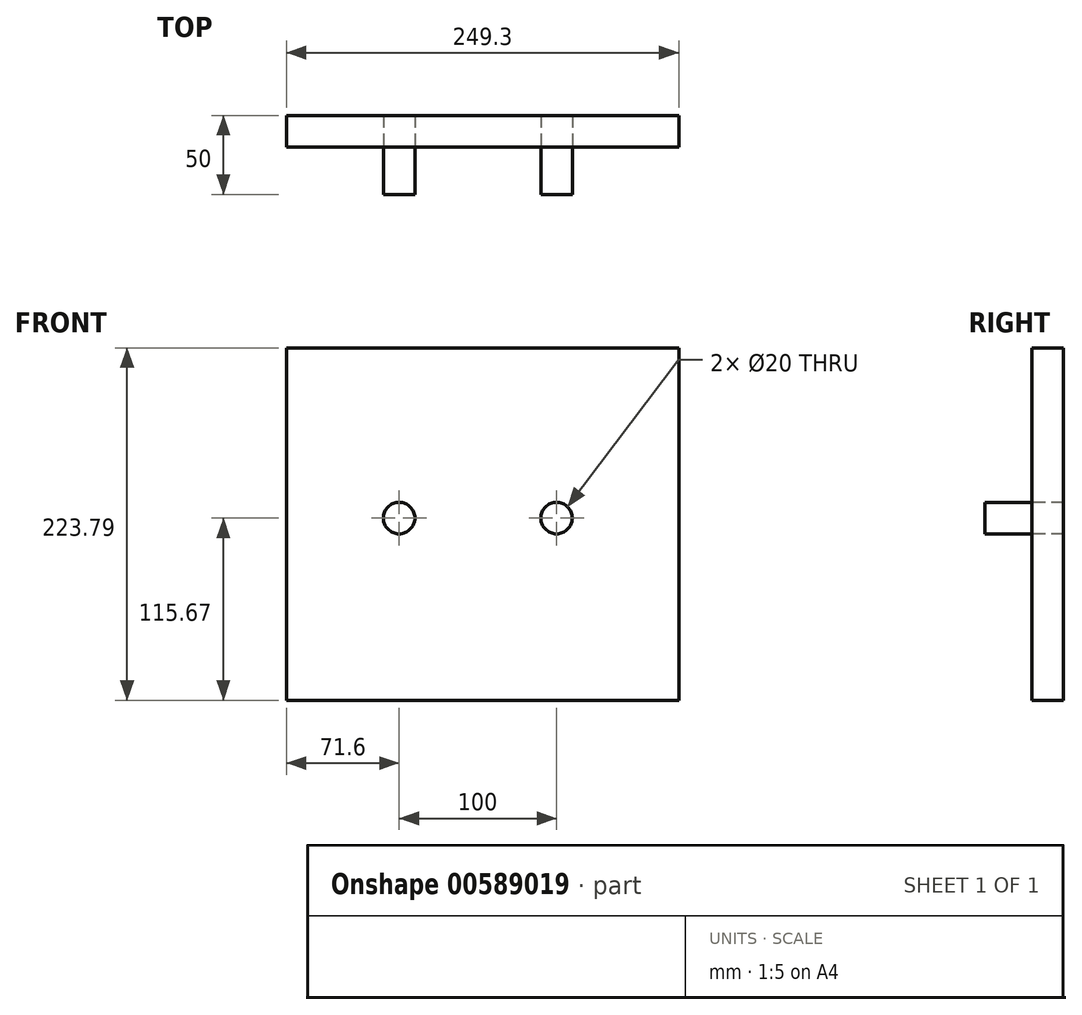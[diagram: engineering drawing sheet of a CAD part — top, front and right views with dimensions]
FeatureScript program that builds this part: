
annotation { "Feature Type Name" : "Feature", "Feature Type Description" : "" }
export const myFeature = defineFeature(function(context is Context, id is Id, definition is map)
    precondition{}
    {
        {
            var Q0;
            Q0=qCreatedBy(makeId("Front.planeOp"),FACE);
            var sketch = newSketch(context, id + "F0", { "sketchPlane" : qUnion([Q0])});
            skCircle(sketch, "E0", {"center": v(0, 0) * mm, "radius": 10 * mm});
            skCircle(sketch, "E1", {"center": v(100, 0) * mm, "radius": 10 * mm});
            skLineSegment(sketch, "E2.bottom", {"start": v(-71.6, 108.12) * mm, "end": v(177.7, 108.12) * mm});
            skLineSegment(sketch, "E2.top", {"start": v(-71.6, -115.67) * mm, "end": v(177.7, -115.67) * mm});
            skLineSegment(sketch, "E2.left", {"start": v(-71.6, 108.12) * mm, "end": v(-71.6, -115.67) * mm});
            skLineSegment(sketch, "E2.right", {"start": v(177.7, 108.12) * mm, "end": v(177.7, -115.67) * mm});
            skSolve(sketch);
        }
        {
            var Q0;
            Q0=makeQuery(id+"F0.imprint","IMPRINT",FACE,{"disambiguationData":[TD([[makeQuery(id+"F0.imprint","IMPRINT",EDGE,{"derivedFrom":sQuery(id+"F0.wireOp",EDGE,"E1")}),1.0]])]});
            var Q1;
            Q1=makeQuery(id+"F0.imprint","IMPRINT",FACE,{"disambiguationData":[TD([[makeQuery(id+"F0.imprint","IMPRINT",EDGE,{"derivedFrom":sQuery(id+"F0.wireOp",EDGE,"E0")}),1.0]])]});
            extrude(context, id + "F1", {"entities" : qUnion([Q0, Q1]), "depth" : 30 * mm, "offsetDistance" : 25.4 * mm});
        }
        {
            var Q0;
            Q0 = qSketchRegion(id + "F0", true);
            extrude(context, id + "F2", {"entities" : qUnion([Q0]), "oppositeDirection" : true, "depth" : 20 * mm, "offsetDistance" : 25.4 * mm});
        }
    });
